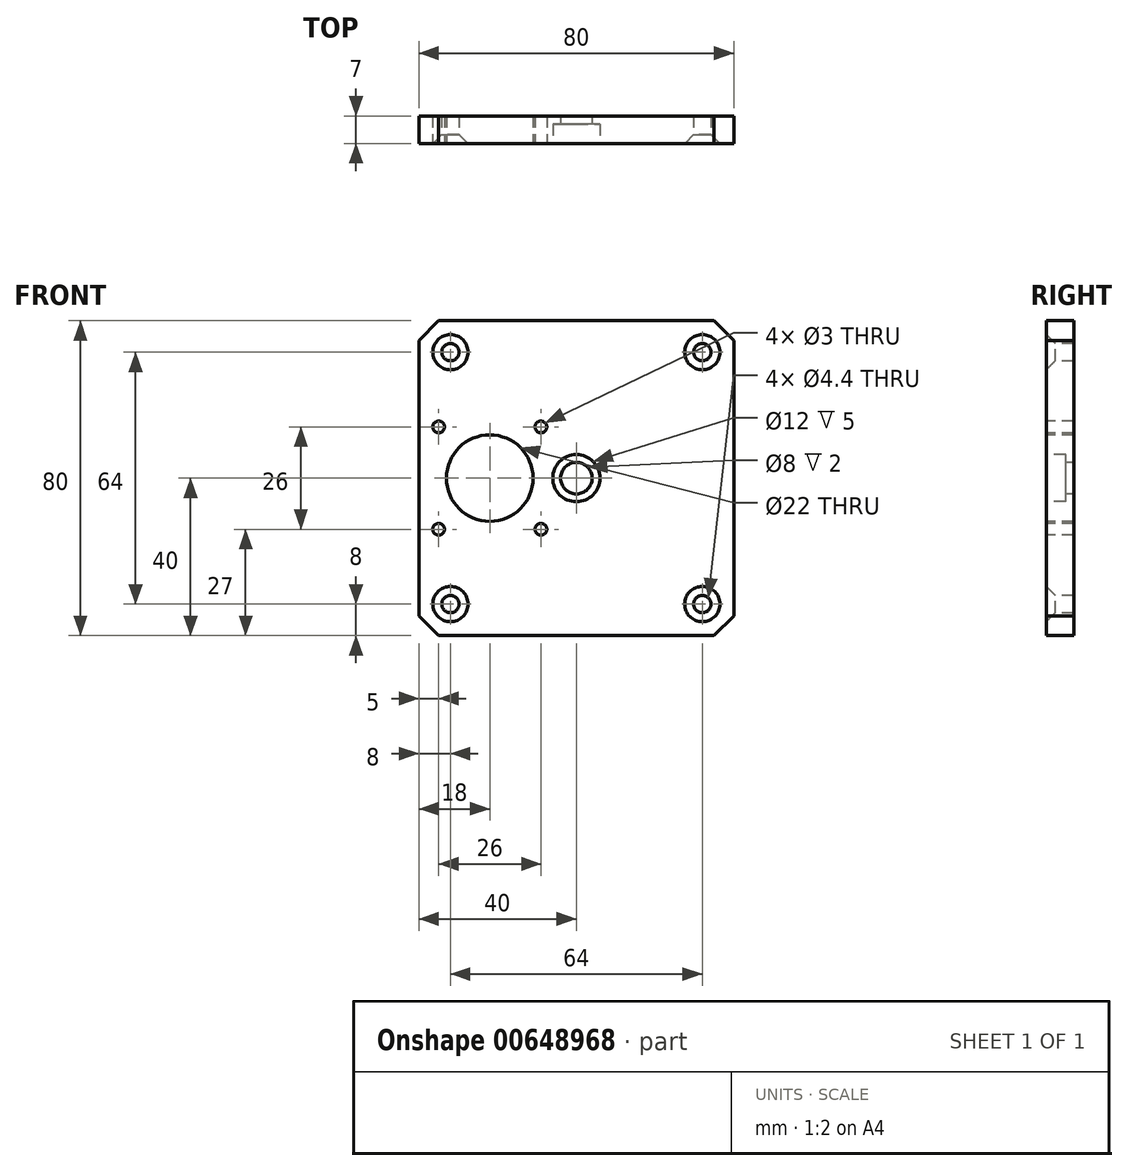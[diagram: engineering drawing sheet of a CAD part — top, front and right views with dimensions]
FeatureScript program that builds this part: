
annotation { "Feature Type Name" : "Feature", "Feature Type Description" : "" }
export const myFeature = defineFeature(function(context is Context, id is Id, definition is map)
    precondition{}
    {
        {
            var Q0;
            Q0=qCreatedBy(makeId("Front.planeOp"),FACE);
            var sketch = newSketch(context, id + "F0", { "sketchPlane" : qUnion([Q0])});
            skLineSegment(sketch, "E0.bottom", {"start": v(-40, 40) * mm, "end": v(40, 40) * mm});
            skLineSegment(sketch, "E0.top", {"start": v(-40, -40) * mm, "end": v(40, -40) * mm});
            skLineSegment(sketch, "E0.left", {"start": v(-40, 40) * mm, "end": v(-40, -40) * mm});
            skLineSegment(sketch, "E0.right", {"start": v(40, 40) * mm, "end": v(40, -40) * mm});
            skPoint(sketch, "E0.middle", {"position": v(0, 0) * mm});
            skSolve(sketch);
        }
        {
            var Q0;
            Q0 = qSketchRegion(id + "F0", true);
            extrude(context, id + "F1", {"entities" : qUnion([Q0]), "depth" : 7 * mm, "offsetDistance" : 25 * mm});
        }
        {
            var Q0;
            Q0=makeQuery(id+"F1.opExtrude","CAP_FACE",FACE,{"disambiguationData":[OSD([sQuery(id+"F0.wireOp",EDGE,"E0.bottom"),sQuery(id+"F0.wireOp",EDGE,"E0.top"),sQuery(id+"F0.wireOp",EDGE,"E0.left"),sQuery(id+"F0.wireOp",EDGE,"E0.right")])],"isStart":false});
            var sketch = newSketch(context, id + "F2", { "sketchPlane" : qUnion([Q0])});
            skCircle(sketch, "E1", {"center": v(0, 0) * mm, "radius": 6 * mm});
            skSolve(sketch);
        }
        {
            var Q0;
            Q0 = qSketchRegion(id + "F2", true);
            extrude(context, id + "F3", {"entities" : qUnion([Q0]), "operationType" : NewBodyOperationType.REMOVE, "oppositeDirection" : true, "depth" : 5 * mm, "offsetDistance" : 25 * mm});
        }
        {
            var Q0;
            Q0=makeQuery(id+"F3.boolean.opBoolean","COPY",FACE,{"derivedFrom":makeQuery(id+"F3.opExtrude","CAP_FACE",FACE,{"disambiguationData":[OSD([sQuery(id+"F2.wireOp",EDGE,"E1")])],"isStart":false})});
            var sketch = newSketch(context, id + "F4", { "sketchPlane" : qUnion([Q0])});
            skCircle(sketch, "E2", {"center": v(0, 0) * mm, "radius": 4 * mm});
            skSolve(sketch);
        }
        {
            var Q0;
            Q0 = qSketchRegion(id + "F4", true);
            extrude(context, id + "F5", {"entities" : qUnion([Q0]), "operationType" : NewBodyOperationType.REMOVE, "endBound" : BoundingType.THROUGH_ALL, "oppositeDirection" : true, "depth" : 25 * mm, "offsetDistance" : 25 * mm});
        }
        {
            var Q0;
            Q0=makeQuery(id+"F1.opExtrude","CAP_FACE",FACE,{"disambiguationData":[OSD([sQuery(id+"F0.wireOp",EDGE,"E0.bottom"),sQuery(id+"F0.wireOp",EDGE,"E0.top"),sQuery(id+"F0.wireOp",EDGE,"E0.left"),sQuery(id+"F0.wireOp",EDGE,"E0.right")])],"isStart":false});
            var sketch = newSketch(context, id + "F6", { "sketchPlane" : qUnion([Q0])});
            skLineSegment(sketch, "E3", {"start": v(0, 0) * mm, "end": v(-40, 0) * mm, "construction": true});
            skCircle(sketch, "E4", {"center": v(-22, 0) * mm, "radius": 11 * mm});
            skCircle(sketch, "E5", {"center": v(-35, 13) * mm, "radius": 1.5 * mm});
            skCircle(sketch, "E6.1.0", {"center": v(-35, -13) * mm, "radius": 1.5 * mm});
            skCircle(sketch, "E6.2.0", {"center": v(-9, -13) * mm, "radius": 1.5 * mm});
            skCircle(sketch, "E6.3.0", {"center": v(-9, 13) * mm, "radius": 1.5 * mm});
            skSolve(sketch);
        }
        {
            var Q0;
            Q0 = qSketchRegion(id + "F6", true);
            extrude(context, id + "F7", {"entities" : qUnion([Q0]), "operationType" : NewBodyOperationType.REMOVE, "endBound" : BoundingType.THROUGH_ALL, "oppositeDirection" : true, "depth" : 25 * mm, "offsetDistance" : 25 * mm});
        }
        {
            var Q0;
            Q0=makeQuery(id+"F1.opExtrude","SWEPT_EDGE",EDGE,{"disambiguationData":[OSD([sQuery(id+"F0.wireOp",EDGE,"E0.bottom"),sQuery(id+"F0.wireOp",EDGE,"E0.left")])]});
            var Q1;
            Q1=makeQuery(id+"F1.opExtrude","SWEPT_EDGE",EDGE,{"disambiguationData":[OSD([sQuery(id+"F0.wireOp",EDGE,"E0.bottom"),sQuery(id+"F0.wireOp",EDGE,"E0.right")])]});
            var Q2;
            Q2=makeQuery(id+"F1.opExtrude","SWEPT_EDGE",EDGE,{"disambiguationData":[OSD([sQuery(id+"F0.wireOp",EDGE,"E0.top"),sQuery(id+"F0.wireOp",EDGE,"E0.left")])]});
            var Q3;
            Q3=makeQuery(id+"F1.opExtrude","SWEPT_EDGE",EDGE,{"disambiguationData":[OSD([sQuery(id+"F0.wireOp",EDGE,"E0.top"),sQuery(id+"F0.wireOp",EDGE,"E0.right")])]});
            chamfer(context, id + "F8", {"entities" : qUnion([Q0, Q1, Q2, Q3]), "width" : 5 * mm, "tangentPropagation" : true});
        }
        {
            var Q0;
            Q0=makeQuery(id+"F1.opExtrude","CAP_FACE",FACE,{"disambiguationData":[OSD([sQuery(id+"F0.wireOp",EDGE,"E0.bottom"),sQuery(id+"F0.wireOp",EDGE,"E0.top"),sQuery(id+"F0.wireOp",EDGE,"E0.left"),sQuery(id+"F0.wireOp",EDGE,"E0.right")])],"isStart":false});
            var sketch = newSketch(context, id + "F9", { "sketchPlane" : qUnion([Q0])});
            skPoint(sketch, "E7", {"position": v(-32, 32) * mm});
            skPoint(sketch, "E8.1.0", {"position": v(-32, -32) * mm});
            skPoint(sketch, "E8.2.0", {"position": v(32, -32) * mm});
            skPoint(sketch, "E8.3.0", {"position": v(32, 32) * mm});
            skPoint(sketch, "E8.center", {"position": v(0, 0) * mm});
            skSolve(sketch);
        }
        {
            var Q0;
            Q0=sQuery(id+"F9.wireOp",VERTEX,"E7");
            var Q1;
            Q1=sQuery(id+"F9.wireOp",VERTEX,"E8.3.0");
            var Q2;
            Q2=sQuery(id+"F9.wireOp",VERTEX,"E8.2.0");
            var Q3;
            Q3=sQuery(id+"F9.wireOp",VERTEX,"E8.1.0");
            var Q4;
            Q4=makeQuery(id+"F1.opExtrude","SWEPT_BODY",BODY,{"disambiguationData":[OSD([sQuery(id+"F0.wireOp",EDGE,"E0.bottom"),sQuery(id+"F0.wireOp",EDGE,"E0.top"),sQuery(id+"F0.wireOp",EDGE,"E0.left"),sQuery(id+"F0.wireOp",EDGE,"E0.right")])]});
            hole(context, id + "F10", {"style" : HoleStyle.C_SINK, "endStyle" : HoleEndStyle.THROUGH, "standardTappedOrClearance" : lookupTablePath({ "standard" : "ISO", "fit" : "Normal", "size" : "M4", "type" : "Clearance" }), "standardBlindInLast" : lookupTablePath({ "fit" : "Standard", "standard" : "ISO", "size" : "M4", "type" : "Clearance" }), "holeDiameter" : 4.4 * mm, "cSinkDiameter" : 8.96 * mm, "cSinkAngle" : 90 * degree, "majorDiameter" : 5 * mm, "isTappedThrough" : true, "tappedDepth" : 12 * mm, "tapClearance" : 3, "locations" : qUnion([Q0, Q1, Q2, Q3]), "scope" : qUnion([Q4])});
        }
    });
